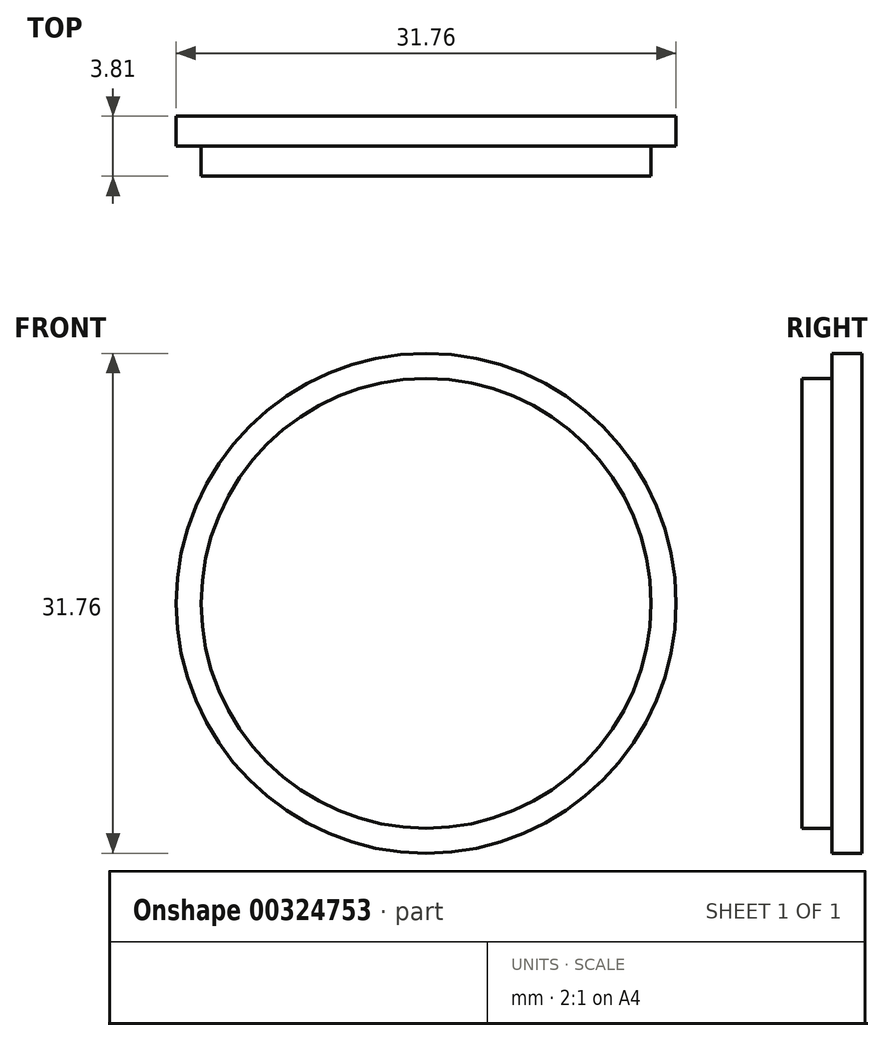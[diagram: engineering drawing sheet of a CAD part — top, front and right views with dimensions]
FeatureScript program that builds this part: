
annotation { "Feature Type Name" : "Feature", "Feature Type Description" : "" }
export const myFeature = defineFeature(function(context is Context, id is Id, definition is map)
    precondition{}
    {
        {
            var Q0;
            Q0=qCreatedBy(makeId("Front.planeOp"),FACE);
            var sketch = newSketch(context, id + "F0", { "sketchPlane" : qUnion([Q0])});
            skCircle(sketch, "E0", {"center": v(0, 0) * mm, "radius": 15.88 * mm});
            skSolve(sketch);
        }
        {
            var Q0;
            Q0=makeQuery(id+"F0.imprint","IMPRINT",FACE,{"disambiguationData":[TD([[makeQuery(id+"F0.imprint","IMPRINT",EDGE,{"derivedFrom":sQuery(id+"F0.wireOp",EDGE,"E0")}),1.0]])]});
            extrude(context, id + "F1", {"entities" : qUnion([Q0]), "depth" : 3.8 * mm, "offsetDistance" : 25.4 * mm});
        }
        {
            var Q0;
            Q0=makeQuery(id+"F1.opExtrude","CAP_FACE",FACE,{"disambiguationData":[OSD([sQuery(id+"F0.wireOp",EDGE,"E0")])],"isStart":false});
            var sketch = newSketch(context, id + "F2", { "sketchPlane" : qUnion([Q0])});
            skCircle(sketch, "E1", {"center": v(0, 0) * mm, "radius": 15.88 * mm});
            skCircle(sketch, "E2", {"center": v(0, 0) * mm, "radius": 14.29 * mm});
            skSolve(sketch);
        }
        {
            var Q0;
            Q0=makeQuery(id+"F2.imprint","IMPRINT",FACE,{"disambiguationData":[TD([[makeQuery(id+"F2.imprint","IMPRINT",EDGE,{"derivedFrom":sQuery(id+"F2.wireOp",EDGE,"E1")}),1.0]])]});
            extrude(context, id + "F3", {"entities" : qUnion([Q0]), "operationType" : NewBodyOperationType.REMOVE, "oppositeDirection" : true, "depth" : 1.9 * mm, "offsetDistance" : 25.4 * mm});
        }
    });
